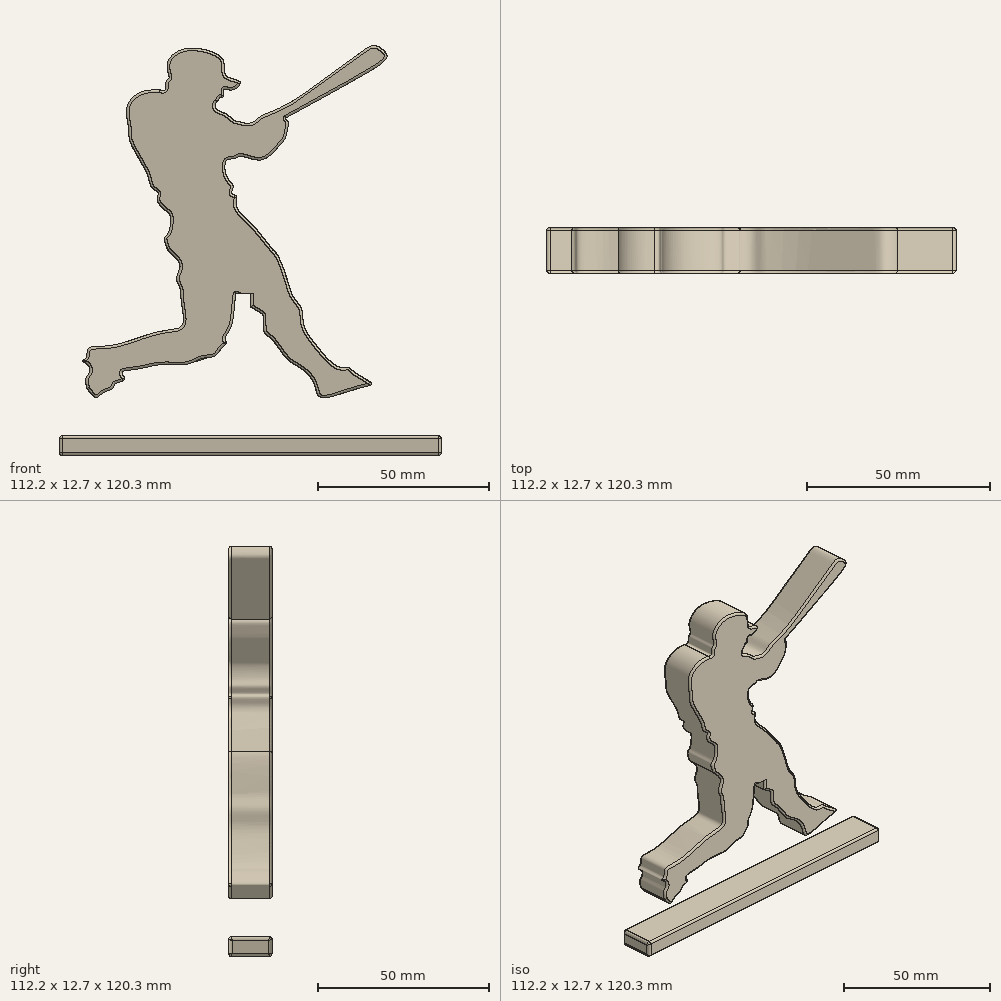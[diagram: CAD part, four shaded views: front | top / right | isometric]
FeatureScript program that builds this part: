
annotation { "Feature Type Name" : "Feature", "Feature Type Description" : "" }
export const myFeature = defineFeature(function(context is Context, id is Id, definition is map)
    precondition{}
    {
        {
            var Q0;
            Q0=qCreatedBy(makeId("Front.planeOp"),FACE);
            var sketch = newSketch(context, id + "F0", { "sketchPlane" : qUnion([Q0])});
            skFitSpline(sketch, "E0", {"points": [v(-44.92, -33.76) * mm, v(-45.22, -30.81) * mm, v(-44.2, -29.08) * mm, v(-44.82, -26.74) * mm, v(-46.24, -25.62) * mm, v(-45.22, -24.8) * mm, v(-44.61, -22.16) * mm, v(-38.1, -21.15) * mm, v(-25.58, -17.48) * mm, v(-19.07, -16.26) * mm, v(-16.83, -14.94) * mm, v(-17.34, -7.71) * mm, v(-17.65, -4.36) * mm, v(-18.67, -1.4) * mm, v(-17.65, 2.05) * mm, v(-21.2, 6.84) * mm], "startDerivative": vector(-14.73, 56.38) * mm, "endDerivative": vector(-64.39, 59.37) * mm});
            skFitSpline(sketch, "E1", {"points": [v(-44.92, -33.76) * mm, v(-42.17, -36.4) * mm, v(-40.03, -34.98) * mm, v(-37.39, -33.76) * mm, v(-36.47, -32.34) * mm, v(-33.83, -31.12) * mm, v(-34.64, -29.18) * mm, v(-30.06, -28.07) * mm, v(-23.14, -26.74) * mm, v(-15.4, -26.64) * mm, v(-11.03, -24.91) * mm, v(-7.27, -24.2) * mm, v(-5.64, -22.27) * mm, v(-4.11, -20.54) * mm, v(-4.42, -19.21) * mm, v(-2.49, -15.24) * mm, v(-1.16, -5.98) * mm, v(0.87, -8.12) * mm, v(6.16, -11.68) * mm, v(6.77, -12.9) * mm, v(7.08, -17.18) * mm, v(9.11, -19.11) * mm, v(13.8, -25.11) * mm, v(17.56, -27.66) * mm, v(21.63, -32.24) * mm, v(23.56, -36.3) * mm, v(34.55, -33.76) * mm, v(38.52, -32.34) * mm, v(33.43, -28.88) * mm, v(31.8, -27.56) * mm, v(29.06, -27.45) * mm, v(21.83, -20.54) * mm, v(18.58, -14.74) * mm, v(17.97, -10.36) * mm, v(15.63, -6.9) * mm, v(14, -2.42) * mm, v(11.05, 5.22) * mm, v(9.72, 6.84) * mm], "startDerivative": vector(113.27, -156.5) * mm, "endDerivative": vector(-66.64, 61.8) * mm});
            skFitSpline(sketch, "E2", {"points": [v(-23.53, 53.85) * mm, v(-28.83, 53.24) * mm, v(-33.2, 48.76) * mm, v(-32.7, 42.45) * mm, v(-32.49, 39.3) * mm, v(-29.23, 32.89) * mm, v(-27, 28.3) * mm, v(-25.77, 25.05) * mm, v(-24.04, 23.52) * mm, v(-24.35, 21.8) * mm, v(-22.72, 19.15) * mm, v(-21.2, 17.93) * mm, v(-20.48, 16.6) * mm, v(-21.2, 11.62) * mm, v(-22.21, 10.4) * mm, v(-21.2, 6.84) * mm], "startDerivative": vector(-65.4, 1.7) * mm, "endDerivative": vector(27.09, -63.71) * mm});
            skFitSpline(sketch, "E3", {"points": [v(9.72, 6.84) * mm, v(2.52, 15.38) * mm, v(-1.16, 19.96) * mm, v(-1.16, 22.71) * mm, v(-2.37, 23.42) * mm, v(-2.06, 25.56) * mm, v(-3.6, 27.8) * mm, v(-4, 32.99) * mm, v(-1.16, 33.8) * mm, v(0, 34.41) * mm, v(6.18, 33.3) * mm, v(11.37, 37.16) * mm, v(13.2, 39.5) * mm, v(13.91, 42.25) * mm, v(14.01, 44.59) * mm, v(13.4, 45.3) * mm, v(13.5, 45.6) * mm], "startDerivative": vector(-61.41, 78.91) * mm, "endDerivative": vector(10.4, 15.04) * mm});
            skFitSpline(sketch, "E4", {"points": [v(-23.53, 53.85) * mm, v(-22.01, 53.85) * mm, v(-21.73, 56.09) * mm, v(-20.86, 57.24) * mm, v(-21.44, 60.98) * mm, v(-17.27, 65.58) * mm, v(-9.06, 65.3) * mm, v(-4.89, 62.27) * mm, v(-4.03, 57.96) * mm, v(0, 56.09) * mm, v(-2.16, 53.85) * mm, v(-4.75, 53.85) * mm, v(-4.89, 51.77) * mm, v(-5.75, 51.62) * mm, v(-6.04, 51.34) * mm, v(-6.62, 50.33) * mm, v(-7.05, 50.04) * mm, v(-7.2, 48.46) * mm, v(-4.6, 47.02) * mm, v(-2.73, 45.72) * mm, v(-1.58, 44.86) * mm, v(0, 44.43) * mm, v(3.17, 44.14) * mm, v(6.05, 46.01) * mm, v(8.92, 47.3) * mm, v(16.26, 51.05) * mm, v(25.9, 57.96) * mm, v(34.83, 64.29) * mm, v(39.29, 66.88) * mm, v(42.17, 65.3) * mm, v(43.03, 63.28) * mm, v(35.06, 57.52) * mm, v(24.07, 51.34) * mm, v(13.5, 45.6) * mm], "startDerivative": vector(98.37, -26.45) * mm, "endDerivative": vector(-195.44, -104.9) * mm});
            skLineSegment(sketch, "E5.bottom", {"start": v(-53.1, -47.63) * mm, "end": v(59.14, -47.63) * mm});
            skLineSegment(sketch, "E5.top", {"start": v(-53.1, -53.39) * mm, "end": v(59.14, -53.39) * mm});
            skLineSegment(sketch, "E5.left", {"start": v(-53.1, -47.63) * mm, "end": v(-53.1, -53.39) * mm});
            skLineSegment(sketch, "E5.right", {"start": v(59.14, -47.63) * mm, "end": v(59.14, -53.39) * mm});
            skLineSegment(sketch, "E6.bottom", {"start": v(-1.16, -5.98) * mm, "end": v(3.02, -5.98) * mm});
            skLineSegment(sketch, "E6.top", {"start": v(-1.16, -47.63) * mm, "end": v(3.02, -47.63) * mm});
            skLineSegment(sketch, "E6.left", {"start": v(-1.16, -5.98) * mm, "end": v(-1.16, -47.63) * mm});
            skLineSegment(sketch, "E6.right", {"start": v(3.02, -5.98) * mm, "end": v(3.02, -47.63) * mm});
            skSolve(sketch);
        }
        {
            var Q0;
            {var subQ7=sQuery(id+"F0.wireOp",EDGE,"E0");Q0=makeQuery(id+"F0.imprint","IMPRINT",FACE,{"disambiguationData":[TD([[makeQuery(id+"F0.imprint","IMPRINT",EDGE,{"derivedFrom":subQ7}),-1.0]])]});}
            var Q1;
            Q1=makeQuery(id+"F0.imprint","IMPRINT",FACE,{"disambiguationData":[TD([[makeQuery(id+"F0.imprint","IMPRINT",EDGE,{"derivedFrom":sQuery(id+"F0.wireOp",EDGE,"E5.top")}),1.0]])]});
            var Q2;
            {var subQ1=sQuery(id+"F0.wireOp",EDGE,"E6.top");Q2=makeQuery(id+"F0.imprint","IMPRINT",FACE,{"disambiguationData":[TD([[makeQuery(id+"F0.imprint","IMPRINT",EDGE,{"derivedFrom":subQ1}),1.0]])]});}
            extrude(context, id + "F1", {"entities" : qUnion([Q0, Q1, Q2]), "depth" : 12.7 * mm, "offsetDistance" : 25.4 * mm});
        }
        {
            var Q0;
            Q0=makeQuery(id+"F1.opExtrude","CAP_EDGE",EDGE,{"disambiguationData":[OSD([sQuery(id+"F0.wireOp",EDGE,"E4")])],"isStart":false});
            var Q1;
            Q1=makeQuery(id+"F1.opExtrude","CAP_EDGE",EDGE,{"disambiguationData":[OSD([sQuery(id+"F0.wireOp",EDGE,"E2")])],"isStart":false});
            var Q2;
            Q2=makeQuery(id+"F1.opExtrude","CAP_EDGE",EDGE,{"disambiguationData":[OSD([sQuery(id+"F0.wireOp",EDGE,"E3")])],"isStart":false});
            var Q3;
            Q3=makeQuery(id+"F1.opExtrude","CAP_EDGE",EDGE,{"disambiguationData":[OSD([sQuery(id+"F0.wireOp",EDGE,"E0")])],"isStart":false});
            var Q4;
            {var subQ0=sQuery(id+"F0.wireOp",EDGE,"E6.bottom");var subQ1=sQuery(id+"F0.wireOp",EDGE,"E1");Q4=makeQuery(id+"F1.opExtrude","CAP_EDGE",EDGE,{"disambiguationData":[OSD([subQ1]),TDD([makeQuery(id+"F0.imprint","IMPRINT",EDGE,{"disambiguationData":[TD([[makeQuery(id+"F0.imprint","INTERSECT",VERTEX,{"derivedFrom":[sQuery(id+"F0.wireOp",EDGE,"E0"),subQ1]}),-1.0]])],"derivedFrom":subQ1}),makeQuery(id+"F0.imprint","IMPRINT",EDGE,{"disambiguationData":[TD([[makeQuery(id+"F0.imprint","INTERSECT",VERTEX,{"derivedFrom":[subQ1,subQ0]}),1.0]])],"derivedFrom":subQ1})])],"isStart":false});}
            var Q5;
            Q5=makeQuery(id+"F1.opExtrude","CAP_EDGE",EDGE,{"disambiguationData":[OSD([sQuery(id+"F0.wireOp",EDGE,"E5.top")])],"isStart":false});
            var Q6;
            {var subQ0=sQuery(id+"F0.wireOp",EDGE,"E1");Q6=makeQuery(id+"F1.opExtrude","CAP_EDGE",EDGE,{"disambiguationData":[OSD([subQ0]),TDD([makeQuery(id+"F0.imprint","IMPRINT",EDGE,{"disambiguationData":[TD([[makeQuery(id+"F0.imprint","INTERSECT",VERTEX,{"derivedFrom":[subQ0,sQuery(id+"F0.wireOp",EDGE,"E3")]}),1.0]])],"derivedFrom":subQ0})])],"isStart":false});}
            var Q7;
            {var subQ0=sQuery(id+"F0.wireOp",EDGE,"E5.bottom");Q7=makeQuery(id+"F1.opExtrude","CAP_EDGE",EDGE,{"disambiguationData":[OSD([subQ0]),TDD([makeQuery(id+"F0.imprint","IMPRINT",EDGE,{"disambiguationData":[TD([[makeQuery(id+"F0.imprint","INTERSECT",VERTEX,{"derivedFrom":[subQ0,sQuery(id+"F0.wireOp",EDGE,"E5.left")]}),-1.0]])],"derivedFrom":subQ0})])],"isStart":false});}
            var Q8;
            {var subQ0=sQuery(id+"F0.wireOp",EDGE,"E6.right");Q8=makeQuery(id+"F1.opExtrude","CAP_EDGE",EDGE,{"disambiguationData":[OSD([subQ0]),TDD([makeQuery(id+"F0.imprint","IMPRINT",EDGE,{"disambiguationData":[TD([[makeQuery(id+"F0.imprint","INTERSECT",VERTEX,{"derivedFrom":[sQuery(id+"F0.wireOp",EDGE,"E1"),subQ0]}),-1.0]])],"derivedFrom":subQ0})])],"isStart":false});}
            var Q9;
            {var subQ0=sQuery(id+"F0.wireOp",EDGE,"E5.bottom");Q9=makeQuery(id+"F1.opExtrude","CAP_EDGE",EDGE,{"disambiguationData":[OSD([subQ0]),TDD([makeQuery(id+"F0.imprint","IMPRINT",EDGE,{"disambiguationData":[TD([[makeQuery(id+"F0.imprint","INTERSECT",VERTEX,{"derivedFrom":[subQ0,sQuery(id+"F0.wireOp",EDGE,"E5.right")]}),1.0]])],"derivedFrom":subQ0})])],"isStart":false});}
            var Q10;
            Q10=makeQuery(id+"F1.opExtrude","CAP_EDGE",EDGE,{"disambiguationData":[OSD([sQuery(id+"F0.wireOp",EDGE,"E6.left")])],"isStart":false});
            fillet(context, id + "F2", {"entities" : qUnion([Q0, Q1, Q2, Q3, Q4, Q5, Q6, Q7, Q8, Q9, Q10]), "radius" : 0.76 * mm, "tangentPropagation" : true, "allowEdgeOverflow" : false});
        }
        {
            var Q0;
            Q0=makeQuery(id+"F1.opExtrude","CAP_EDGE",EDGE,{"disambiguationData":[OSD([sQuery(id+"F0.wireOp",EDGE,"E4")])],"isStart":true});
            var Q1;
            Q1=makeQuery(id+"F1.opExtrude","CAP_EDGE",EDGE,{"disambiguationData":[OSD([sQuery(id+"F0.wireOp",EDGE,"E3")])],"isStart":true});
            var Q2;
            Q2=makeQuery(id+"F1.opExtrude","CAP_EDGE",EDGE,{"disambiguationData":[OSD([sQuery(id+"F0.wireOp",EDGE,"E2")])],"isStart":true});
            var Q3;
            Q3=makeQuery(id+"F1.opExtrude","CAP_EDGE",EDGE,{"disambiguationData":[OSD([sQuery(id+"F0.wireOp",EDGE,"E0")])],"isStart":true});
            var Q4;
            {var subQ0=sQuery(id+"F0.wireOp",EDGE,"E1");Q4=makeQuery(id+"F1.opExtrude","CAP_EDGE",EDGE,{"disambiguationData":[OSD([subQ0]),TDD([makeQuery(id+"F0.imprint","IMPRINT",EDGE,{"disambiguationData":[TD([[makeQuery(id+"F0.imprint","INTERSECT",VERTEX,{"derivedFrom":[subQ0,sQuery(id+"F0.wireOp",EDGE,"E3")]}),1.0]])],"derivedFrom":subQ0})])],"isStart":true});}
            var Q5;
            Q5=makeQuery(id+"F1.opExtrude","CAP_EDGE",EDGE,{"disambiguationData":[OSD([sQuery(id+"F0.wireOp",EDGE,"E6.left")])],"isStart":true});
            var Q6;
            {var subQ0=sQuery(id+"F0.wireOp",EDGE,"E6.bottom");var subQ1=sQuery(id+"F0.wireOp",EDGE,"E1");Q6=makeQuery(id+"F1.opExtrude","CAP_EDGE",EDGE,{"disambiguationData":[OSD([subQ1]),TDD([makeQuery(id+"F0.imprint","IMPRINT",EDGE,{"disambiguationData":[TD([[makeQuery(id+"F0.imprint","INTERSECT",VERTEX,{"derivedFrom":[sQuery(id+"F0.wireOp",EDGE,"E0"),subQ1]}),-1.0]])],"derivedFrom":subQ1}),makeQuery(id+"F0.imprint","IMPRINT",EDGE,{"disambiguationData":[TD([[makeQuery(id+"F0.imprint","INTERSECT",VERTEX,{"derivedFrom":[subQ1,subQ0]}),1.0]])],"derivedFrom":subQ1})])],"isStart":true});}
            var Q7;
            {var subQ0=sQuery(id+"F0.wireOp",EDGE,"E5.bottom");Q7=makeQuery(id+"F1.opExtrude","CAP_EDGE",EDGE,{"disambiguationData":[OSD([subQ0]),TDD([makeQuery(id+"F0.imprint","IMPRINT",EDGE,{"disambiguationData":[TD([[makeQuery(id+"F0.imprint","INTERSECT",VERTEX,{"derivedFrom":[subQ0,sQuery(id+"F0.wireOp",EDGE,"E5.left")]}),-1.0]])],"derivedFrom":subQ0})])],"isStart":true});}
            var Q8;
            {var subQ0=sQuery(id+"F0.wireOp",EDGE,"E5.bottom");Q8=makeQuery(id+"F1.opExtrude","CAP_EDGE",EDGE,{"disambiguationData":[OSD([subQ0]),TDD([makeQuery(id+"F0.imprint","IMPRINT",EDGE,{"disambiguationData":[TD([[makeQuery(id+"F0.imprint","INTERSECT",VERTEX,{"derivedFrom":[subQ0,sQuery(id+"F0.wireOp",EDGE,"E5.right")]}),1.0]])],"derivedFrom":subQ0})])],"isStart":true});}
            var Q9;
            {var subQ0=sQuery(id+"F0.wireOp",EDGE,"E6.right");Q9=makeQuery(id+"F1.opExtrude","CAP_EDGE",EDGE,{"disambiguationData":[OSD([subQ0]),TDD([makeQuery(id+"F0.imprint","IMPRINT",EDGE,{"disambiguationData":[TD([[makeQuery(id+"F0.imprint","INTERSECT",VERTEX,{"derivedFrom":[sQuery(id+"F0.wireOp",EDGE,"E1"),subQ0]}),-1.0]])],"derivedFrom":subQ0})])],"isStart":true});}
            var Q10;
            Q10=makeQuery(id+"F1.opExtrude","CAP_EDGE",EDGE,{"disambiguationData":[OSD([sQuery(id+"F0.wireOp",EDGE,"E5.top")])],"isStart":true});
            fillet(context, id + "F3", {"entities" : qUnion([Q0, Q1, Q2, Q3, Q4, Q5, Q6, Q7, Q8, Q9, Q10]), "radius" : 0.76 * mm, "tangentPropagation" : true, "allowEdgeOverflow" : false});
        }
        {
            var Q0;
            Q0=makeQuery(id+"F1.opExtrude","SWEPT_FACE",FACE,{"disambiguationData":[OSD([sQuery(id+"F0.wireOp",EDGE,"E2")])]});
            var Q1;
            Q1=makeQuery(id+"F1.opExtrude","SWEPT_FACE",FACE,{"disambiguationData":[OSD([sQuery(id+"F0.wireOp",EDGE,"E0")])]});
            var Q2;
            Q2=makeQuery(id+"F1.opExtrude","SWEPT_FACE",FACE,{"disambiguationData":[OSD([sQuery(id+"F0.wireOp",EDGE,"E4")])]});
            var Q3;
            Q3=makeQuery(id+"F1.opExtrude","SWEPT_FACE",FACE,{"disambiguationData":[OSD([sQuery(id+"F0.wireOp",EDGE,"E3")])]});
            var Q4;
            {var subQ0=sQuery(id+"F0.wireOp",EDGE,"E1");Q4=makeQuery(id+"F1.opExtrude","SWEPT_FACE",FACE,{"disambiguationData":[OSD([subQ0]),TDD([makeQuery(id+"F0.imprint","IMPRINT",EDGE,{"disambiguationData":[TD([[makeQuery(id+"F0.imprint","INTERSECT",VERTEX,{"derivedFrom":[subQ0,sQuery(id+"F0.wireOp",EDGE,"E3")]}),1.0]])],"derivedFrom":subQ0})])]});}
            var Q5;
            {var subQ0=sQuery(id+"F0.wireOp",EDGE,"E6.bottom");var subQ1=sQuery(id+"F0.wireOp",EDGE,"E1");var subQ3=makeQuery(id+"F0.imprint","IMPRINT",EDGE,{"disambiguationData":[TD([[makeQuery(id+"F0.imprint","INTERSECT",VERTEX,{"derivedFrom":[subQ1,subQ0]}),1.0]])],"derivedFrom":subQ1});var subQ4=makeQuery(id+"F0.imprint","IMPRINT",EDGE,{"disambiguationData":[TD([[makeQuery(id+"F0.imprint","INTERSECT",VERTEX,{"derivedFrom":[sQuery(id+"F0.wireOp",EDGE,"E0"),subQ1]}),-1.0]])],"derivedFrom":subQ1});Q5=makeQuery(id+"F2.opFillet","BLEND_EDGE",EDGE,{"disambiguationData":[OD(2.0)],"blendedFrom":[makeQuery(id+"F1.opExtrude","CAP_EDGE",EDGE,{"disambiguationData":[OSD([subQ1]),TDD([subQ4,subQ3])],"isStart":false}),makeQuery(id+"F1.opExtrude","SWEPT_FACE",FACE,{"disambiguationData":[OSD([subQ1]),TDD([subQ4,subQ3])]})],"blendedInto":[makeQuery(id+"F1.opExtrude","SWEPT_FACE",FACE,{"disambiguationData":[OSD([subQ1]),TDD([subQ4,subQ3])]})]});}
            var Q6;
            {var subQ0=sQuery(id+"F0.wireOp",EDGE,"E6.left");var subQ1=sQuery(id+"F0.wireOp",EDGE,"E5.left");var subQ2=sQuery(id+"F0.wireOp",EDGE,"E5.bottom");Q6=makeQuery(id+"F2.opFillet","BLEND_EDGE",EDGE,{"blendedFrom":[makeQuery(id+"F1.opExtrude","CAP_EDGE",EDGE,{"disambiguationData":[OSD([subQ2]),TDD([makeQuery(id+"F0.imprint","IMPRINT",EDGE,{"disambiguationData":[TD([[makeQuery(id+"F0.imprint","INTERSECT",VERTEX,{"derivedFrom":[subQ2,subQ1]}),-1.0]])],"derivedFrom":subQ2})])],"isStart":false}),makeQuery(id+"F1.opExtrude","CAP_FACE",FACE,{"disambiguationData":[OSD([sQuery(id+"F0.wireOp",EDGE,"E1"),subQ2,sQuery(id+"F0.wireOp",EDGE,"E5.top"),subQ1,sQuery(id+"F0.wireOp",EDGE,"E5.right"),sQuery(id+"F0.wireOp",EDGE,"E6.bottom"),subQ0,sQuery(id+"F0.wireOp",EDGE,"E6.right")])],"isStart":false})],"blendedInto":[makeQuery(id+"F1.opExtrude","CAP_FACE",FACE,{"disambiguationData":[OSD([sQuery(id+"F0.wireOp",EDGE,"E1"),subQ2,sQuery(id+"F0.wireOp",EDGE,"E5.top"),subQ1,sQuery(id+"F0.wireOp",EDGE,"E5.right"),sQuery(id+"F0.wireOp",EDGE,"E6.bottom"),subQ0,sQuery(id+"F0.wireOp",EDGE,"E6.right")])],"isStart":false})]});}
            var Q7;
            Q7=makeQuery(id+"F1.opExtrude","SWEPT_FACE",FACE,{"disambiguationData":[OSD([sQuery(id+"F0.wireOp",EDGE,"E5.top")])]});
            var Q8;
            {var subQ0=sQuery(id+"F0.wireOp",EDGE,"E6.bottom");var subQ1=sQuery(id+"F0.wireOp",EDGE,"E1");Q8=makeQuery(id+"F1.opExtrude","SWEPT_FACE",FACE,{"disambiguationData":[OSD([subQ1]),TDD([makeQuery(id+"F0.imprint","IMPRINT",EDGE,{"disambiguationData":[TD([[makeQuery(id+"F0.imprint","INTERSECT",VERTEX,{"derivedFrom":[sQuery(id+"F0.wireOp",EDGE,"E0"),subQ1]}),-1.0]])],"derivedFrom":subQ1}),makeQuery(id+"F0.imprint","IMPRINT",EDGE,{"disambiguationData":[TD([[makeQuery(id+"F0.imprint","INTERSECT",VERTEX,{"derivedFrom":[subQ1,subQ0]}),1.0]])],"derivedFrom":subQ1})])]});}
            fillet(context, id + "F4", {"entities" : qUnion([Q0, Q1, Q2, Q3, Q4, Q5, Q6, Q7, Q8]), "radius" : 1.02 * mm, "tangentPropagation" : true, "allowEdgeOverflow" : false});
        }
    });
